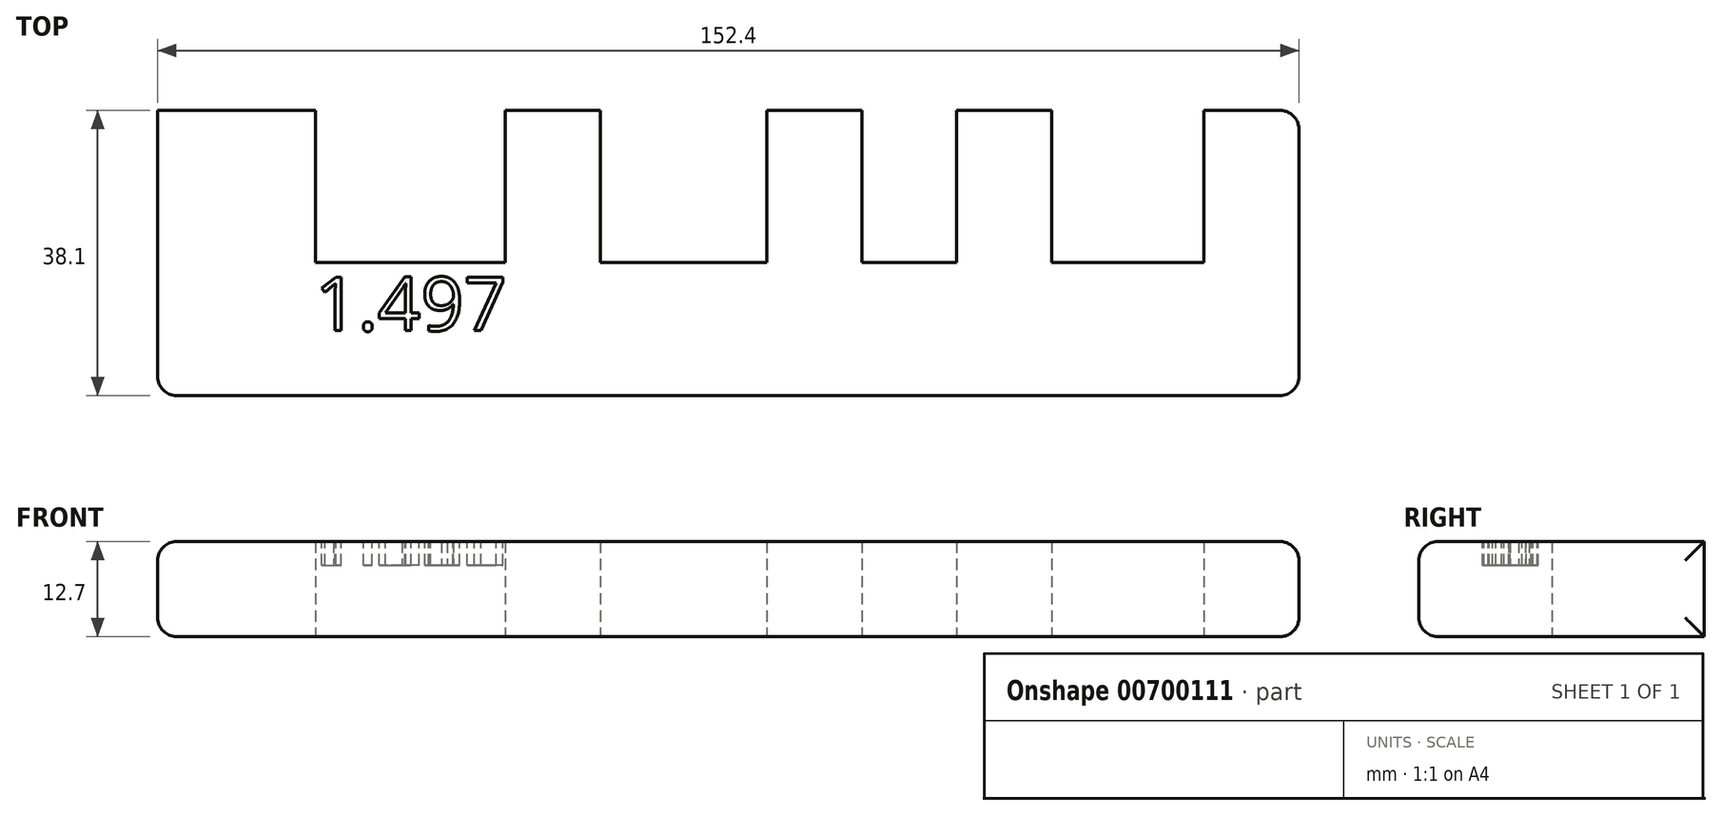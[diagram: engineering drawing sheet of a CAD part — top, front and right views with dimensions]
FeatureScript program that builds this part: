
annotation { "Feature Type Name" : "Feature", "Feature Type Description" : "" }
export const myFeature = defineFeature(function(context is Context, id is Id, definition is map)
    precondition{}
    {
        {
            var Q0;
            Q0=qCreatedBy(makeId("Top.planeOp"),FACE);
            var sketch = newSketch(context, id + "F0", { "sketchPlane" : qUnion([Q0])});
            skLineSegment(sketch, "E0.bottom", {"start": v(76.2, -19.05) * mm, "end": v(-76.2, -19.05) * mm});
            skLineSegment(sketch, "E0.top", {"start": v(76.2, 19.05) * mm, "end": v(63.5, 19.05) * mm});
            skLineSegment(sketch, "E0.left", {"start": v(76.2, -19.05) * mm, "end": v(76.2, 19.05) * mm});
            skLineSegment(sketch, "E0.right", {"start": v(-76.2, -19.05) * mm, "end": v(-76.2, 19.05) * mm});
            skPoint(sketch, "E0.middle", {"position": v(0, 0) * mm});
            skLineSegment(sketch, "E1.top", {"start": v(-55.12, -1.27) * mm, "end": v(-17.1, -1.27) * mm});
            skLineSegment(sketch, "E1.left", {"start": v(-55.12, 19.05) * mm, "end": v(-55.12, -1.27) * mm});
            skLineSegment(sketch, "E1.right", {"start": v(-17.1, 19.05) * mm, "end": v(-17.1, -1.27) * mm});
            skLineSegment(sketch, "E2.top", {"start": v(-29.8, -1.27) * mm, "end": v(5.16, -1.27) * mm});
            skLineSegment(sketch, "E2.left", {"start": v(-29.8, 19.05) * mm, "end": v(-29.8, -1.27) * mm});
            skLineSegment(sketch, "E2.right", {"start": v(5.16, 19.05) * mm, "end": v(5.16, -1.27) * mm});
            skLineSegment(sketch, "E3.top", {"start": v(17.86, -1.27) * mm, "end": v(30.5, -1.27) * mm});
            skLineSegment(sketch, "E3.left", {"start": v(17.86, 19.05) * mm, "end": v(17.86, -1.27) * mm});
            skLineSegment(sketch, "E3.right", {"start": v(30.5, 19.05) * mm, "end": v(30.5, -1.27) * mm});
            skLineSegment(sketch, "E4.top", {"start": v(43.2, -1.27) * mm, "end": v(63.5, -1.27) * mm});
            skLineSegment(sketch, "E4.left", {"start": v(43.2, 19.05) * mm, "end": v(43.2, -1.27) * mm});
            skLineSegment(sketch, "E4.right", {"start": v(63.5, 19.05) * mm, "end": v(63.5, -1.27) * mm});
            skLineSegment(sketch, "E5.left", {"start": v(-55.12, -1.27) * mm, "end": v(-55.12, -1.27) * mm});
            skLineSegment(sketch, "E5.right", {"start": v(-17.1, -1.27) * mm, "end": v(-17.1, -1.27) * mm});
            skLineSegment(sketch, "E6.trimOffspring", {"start": v(43.2, 19.05) * mm, "end": v(30.5, 19.05) * mm});
            skLineSegment(sketch, "E7.trimOffspring", {"start": v(17.86, 19.05) * mm, "end": v(5.16, 19.05) * mm});
            skLineSegment(sketch, "E8.trimOffspring", {"start": v(-17.1, 19.05) * mm, "end": v(-29.8, 19.05) * mm});
            skLineSegment(sketch, "E9.trimOffspring", {"start": v(-55.12, 19.05) * mm, "end": v(-76.2, 19.05) * mm});
            skSolve(sketch);
        }
        {
            var Q0;
            Q0 = qSketchRegion(id + "F0", true);
            extrude(context, id + "F1", {"entities" : qUnion([Q0]), "endBound" : BoundingType.SYMMETRIC, "depth" : 12.7 * mm, "offsetDistance" : 25.4 * mm});
        }
        {
            var Q0;
            Q0=makeQuery(id+"F1.opExtrude","CAP_FACE",FACE,{"disambiguationData":[OSD([sQuery(id+"F0.wireOp",EDGE,"E0.bottom"),sQuery(id+"F0.wireOp",EDGE,"E0.top"),sQuery(id+"F0.wireOp",EDGE,"E0.left"),sQuery(id+"F0.wireOp",EDGE,"E0.right"),sQuery(id+"F0.wireOp",EDGE,"E1.left"),sQuery(id+"F0.wireOp",EDGE,"E1.right"),sQuery(id+"F0.wireOp",EDGE,"E2.top"),sQuery(id+"F0.wireOp",EDGE,"E2.left"),sQuery(id+"F0.wireOp",EDGE,"E2.right"),sQuery(id+"F0.wireOp",EDGE,"E3.top"),sQuery(id+"F0.wireOp",EDGE,"E3.left"),sQuery(id+"F0.wireOp",EDGE,"E3.right"),sQuery(id+"F0.wireOp",EDGE,"E4.top"),sQuery(id+"F0.wireOp",EDGE,"E4.left"),sQuery(id+"F0.wireOp",EDGE,"E4.right"),sQuery(id+"F0.wireOp",EDGE,"E1.top"),sQuery(id+"F0.wireOp",EDGE,"E6.trimOffspring"),sQuery(id+"F0.wireOp",EDGE,"E7.trimOffspring"),sQuery(id+"F0.wireOp",EDGE,"E8.trimOffspring"),sQuery(id+"F0.wireOp",EDGE,"E9.trimOffspring")])],"isStart":false});
            var sketch = newSketch(context, id + "F2", { "sketchPlane" : qUnion([Q0])});
            skText(sketch, "E10", { "text": "1.497\n", "fontName": "OpenSans-Regular.ttf"});
            const initialGuessF2  = {"E10": [-0.0552, -0.01038, 1, 0, 0.00722]};
            skSetInitialGuess(sketch, initialGuessF2);
            skSolve(sketch);
        }
        {
            var Q0;
            Q0 = qSketchRegion(id + "F2", true);
            extrude(context, id + "F3", {"entities" : qUnion([Q0]), "operationType" : NewBodyOperationType.REMOVE, "oppositeDirection" : true, "depth" : 3.17 * mm, "offsetDistance" : 25.4 * mm});
        }
        {
            var Q0;
            Q0=makeQuery(id+"F1.opExtrude","CAP_EDGE",EDGE,{"disambiguationData":[OSD([sQuery(id+"F0.wireOp",EDGE,"E0.right")])],"isStart":false});
            var Q1;
            Q1=makeQuery(id+"F1.opExtrude","CAP_EDGE",EDGE,{"disambiguationData":[OSD([sQuery(id+"F0.wireOp",EDGE,"E0.bottom")])],"isStart":false});
            var Q2;
            Q2=makeQuery(id+"F1.opExtrude","CAP_EDGE",EDGE,{"disambiguationData":[OSD([sQuery(id+"F0.wireOp",EDGE,"E0.left")])],"isStart":false});
            var Q3;
            Q3=makeQuery(id+"F1.opExtrude","CAP_EDGE",EDGE,{"disambiguationData":[OSD([sQuery(id+"F0.wireOp",EDGE,"E0.left")])],"isStart":true});
            var Q4;
            Q4=makeQuery(id+"F1.opExtrude","SWEPT_FACE",FACE,{"disambiguationData":[OSD([sQuery(id+"F0.wireOp",EDGE,"E0.left")])]});
            var Q5;
            Q5=makeQuery(id+"F1.opExtrude","CAP_EDGE",EDGE,{"disambiguationData":[OSD([sQuery(id+"F0.wireOp",EDGE,"E0.bottom")])],"isStart":true});
            var Q6;
            Q6=makeQuery(id+"F1.opExtrude","SWEPT_EDGE",EDGE,{"disambiguationData":[OSD([sQuery(id+"F0.wireOp",EDGE,"E0.bottom"),sQuery(id+"F0.wireOp",EDGE,"E0.right")])]});
            var Q7;
            Q7=makeQuery(id+"F1.opExtrude","CAP_EDGE",EDGE,{"disambiguationData":[OSD([sQuery(id+"F0.wireOp",EDGE,"E0.right")])],"isStart":true});
            fillet(context, id + "F4", {"entities" : qUnion([Q0, Q1, Q2, Q3, Q4, Q5, Q6, Q7]), "radius" : 2.54 * mm, "tangentPropagation" : true, "allowEdgeOverflow" : false});
        }
    });
